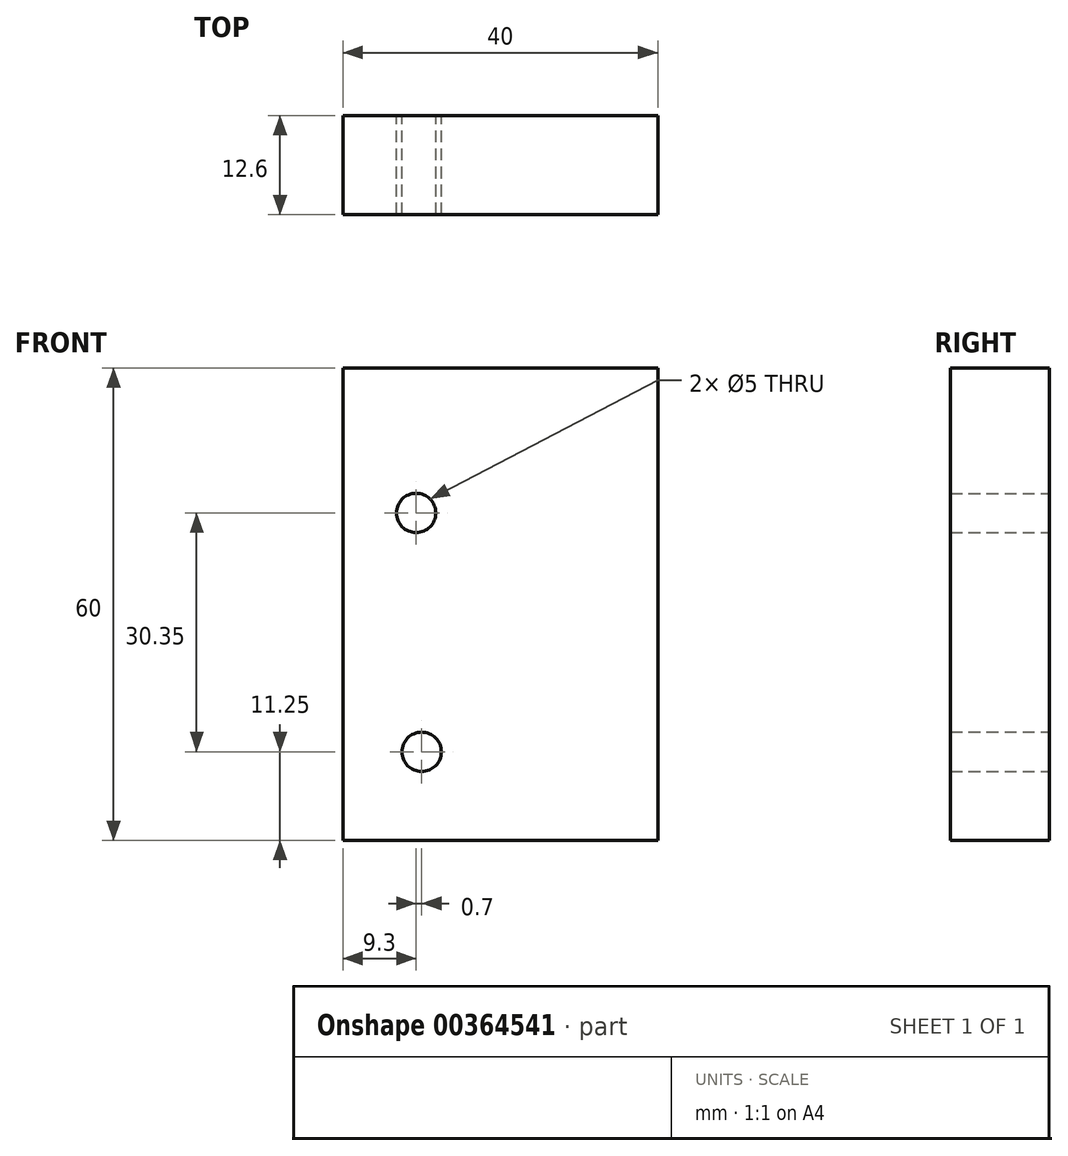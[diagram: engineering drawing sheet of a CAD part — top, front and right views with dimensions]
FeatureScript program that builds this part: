
annotation { "Feature Type Name" : "Feature", "Feature Type Description" : "" }
export const myFeature = defineFeature(function(context is Context, id is Id, definition is map)
    precondition{}
    {
        {
            var Q0;
            Q0=qCreatedBy(makeId("Front.planeOp"),FACE);
            var sketch = newSketch(context, id + "F0", { "sketchPlane" : qUnion([Q0])});
            skLineSegment(sketch, "E0.bottom", {"start": v(0, 0) * mm, "end": v(40, 0) * mm});
            skLineSegment(sketch, "E0.top", {"start": v(0, 60) * mm, "end": v(40, 60) * mm});
            skLineSegment(sketch, "E0.left", {"start": v(0, 0) * mm, "end": v(0, 60) * mm});
            skLineSegment(sketch, "E0.right", {"start": v(40, 0) * mm, "end": v(40, 60) * mm});
            skLineSegment(sketch, "E1", {"start": v(20, 60) * mm, "end": v(20, 0) * mm, "construction": true});
            skLineSegment(sketch, "E2", {"start": v(10, 60) * mm, "end": v(10, 0) * mm, "construction": true});
            skCircle(sketch, "E3", {"center": v(10, 11.25) * mm, "radius": 2.5 * mm});
            skCircle(sketch, "E4.0.1.0", {"center": v(9.3, 41.6) * mm, "radius": 2.5 * mm});
            skLineSegment(sketch, "E4.direction1", {"start": v(10, 11.25) * mm, "end": v(34.8, 11.25) * mm, "construction": true});
            skLineSegment(sketch, "E4.direction2", {"start": v(10, 11.25) * mm, "end": v(9.3, 41.6) * mm, "construction": true});
            skSolve(sketch);
        }
        {
            var Q0;
            Q0=makeQuery(id+"F0.imprint","IMPRINT",FACE,{"disambiguationData":[TD([[makeQuery(id+"F0.imprint","IMPRINT",EDGE,{"derivedFrom":sQuery(id+"F0.wireOp",EDGE,"E0.bottom")}),1.0]])]});
            extrude(context, id + "F1", {"entities" : qUnion([Q0]), "depth" : 12.6 * mm});
        }
    });
